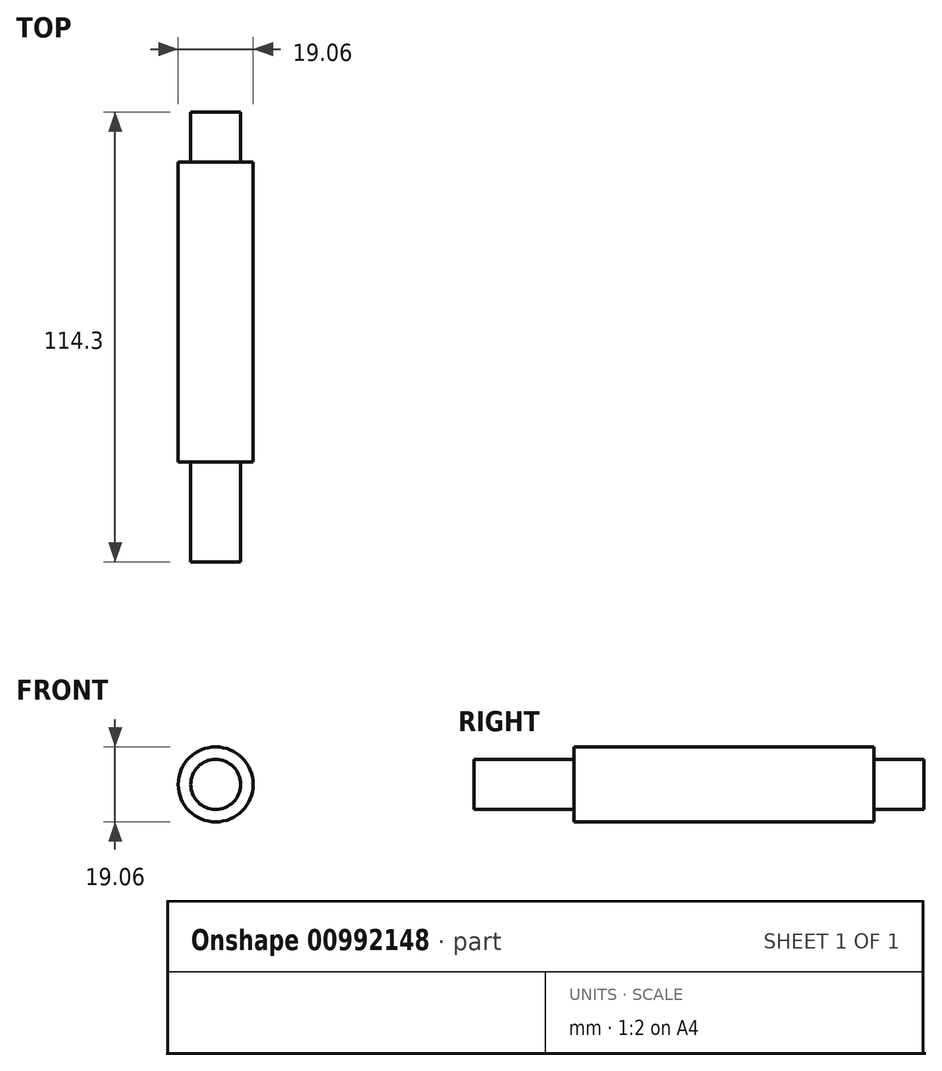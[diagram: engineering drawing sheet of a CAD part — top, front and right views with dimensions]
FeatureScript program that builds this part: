
annotation { "Feature Type Name" : "Feature", "Feature Type Description" : "" }
export const myFeature = defineFeature(function(context is Context, id is Id, definition is map)
    precondition{}
    {
        {
            var Q0;
            Q0=qCreatedBy(makeId("Front.planeOp"),FACE);
            var sketch = newSketch(context, id + "F0", { "sketchPlane" : qUnion([Q0])});
            skCircle(sketch, "E0", {"center": v(0, 0) * mm, "radius": 9.53 * mm});
            skCircle(sketch, "E1", {"center": v(0, 0) * mm, "radius": 6.35 * mm});
            skSolve(sketch);
        }
        {
            var Q0;
            Q0=makeQuery(id+"F0.imprint","IMPRINT",FACE,{"disambiguationData":[TD([[makeQuery(id+"F0.imprint","IMPRINT",EDGE,{"derivedFrom":sQuery(id+"F0.wireOp",EDGE,"E1")}),1.0]])]});
            var Q1;
            Q1=sQuery(id+"F0.wireOp",EDGE,"E1");
            extrude(context, id + "F1", {"entities" : qUnion([Q0]), "surfaceEntities" : qUnion([Q1]), "depth" : 114.3 * mm, "offsetDistance" : 25.4 * mm});
        }
        {
            var Q0;
            Q0=makeQuery(id+"F0.imprint","IMPRINT",FACE,{"disambiguationData":[TD([[makeQuery(id+"F0.imprint","IMPRINT",EDGE,{"derivedFrom":sQuery(id+"F0.wireOp",EDGE,"E0")}),1.0]])]});
            var Q1;
            Q1=sQuery(id+"F0.wireOp",EDGE,"E0");
            extrude(context, id + "F2", {"entities" : qUnion([Q0]), "operationType" : NewBodyOperationType.ADD, "surfaceEntities" : qUnion([Q1]), "depth" : 88.9 * mm, "offsetDistance" : 25.4 * mm});
        }
        {
            var Q0;
            Q0=makeQuery(id+"F0.imprint","IMPRINT",FACE,{"disambiguationData":[TD([[makeQuery(id+"F0.imprint","IMPRINT",EDGE,{"derivedFrom":sQuery(id+"F0.wireOp",EDGE,"E0")}),1.0]])]});
            var Q1;
            Q1=sQuery(id+"F0.wireOp",EDGE,"E0");
            extrude(context, id + "F3", {"entities" : qUnion([Q0]), "operationType" : NewBodyOperationType.REMOVE, "surfaceEntities" : qUnion([Q1]), "depth" : 12.7 * mm, "offsetDistance" : 25.4 * mm});
        }
    });
